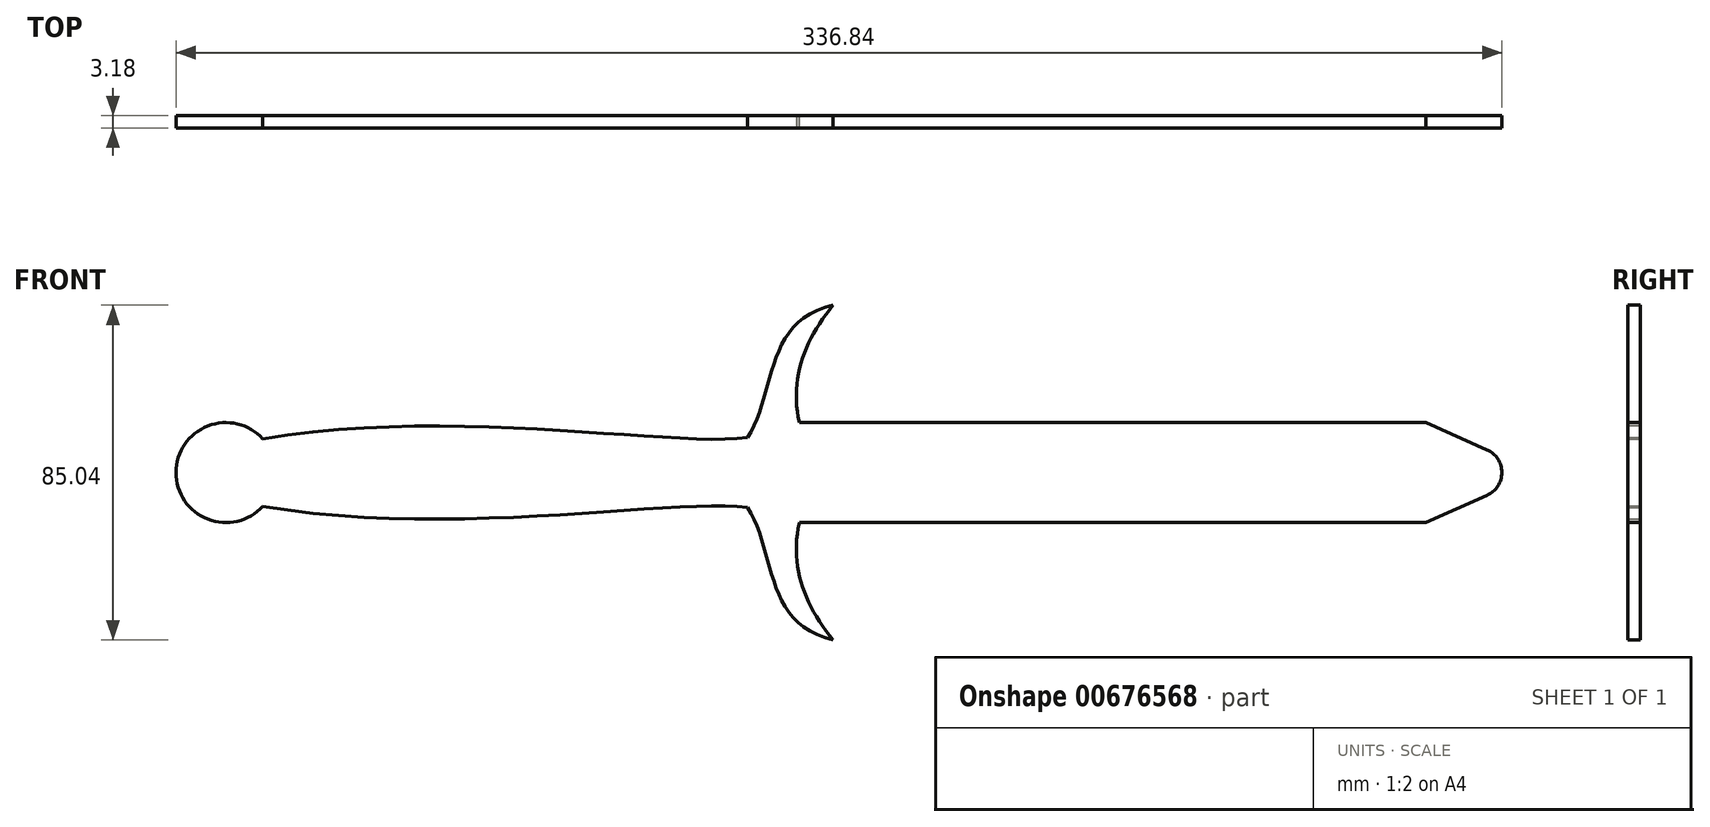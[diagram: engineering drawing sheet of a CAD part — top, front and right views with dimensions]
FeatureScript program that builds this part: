
annotation { "Feature Type Name" : "Feature", "Feature Type Description" : "" }
export const myFeature = defineFeature(function(context is Context, id is Id, definition is map)
    precondition{}
    {
        {
            var Q0;
            Q0=qCreatedBy(makeId("Front.planeOp"),FACE);
            var sketch = newSketch(context, id + "F0", { "sketchPlane" : qUnion([Q0])});
            skLineSegment(sketch, "E0", {"start": v(-145.25, 13.54) * mm, "end": v(159.55, 13.54) * mm, "construction": true});
            skCircle(sketch, "E1", {"center": v(-145.25, 13.54) * mm, "radius": 12.7 * mm});
            skFitSpline(sketch, "E2", {"points": [v(-135.87, 22.1) * mm, v(-12.7, 22.4) * mm], "startDerivative": vector(145, 25.04) * mm, "endDerivative": vector(57.12, 7.62) * mm});
            skFitSpline(sketch, "E3.MirrorCS", {"points": [v(-135.87, 4.98) * mm, v(-12.7, 4.67) * mm], "startDerivative": vector(145, -25.04) * mm, "endDerivative": vector(57.12, -7.62) * mm});
            skFitSpline(sketch, "E4", {"points": [v(-12.7, 22.4) * mm, v(9.02, 56.06) * mm], "startDerivative": vector(21.73, 33.66) * mm, "endDerivative": vector(53.2, 11.82) * mm});
            skFitSpline(sketch, "E5", {"points": [v(9.02, 56.06) * mm, v(3.11, 18.63) * mm], "startDerivative": vector(-27.07, -32.5) * mm, "endDerivative": vector(20.1, -42.56) * mm});
            skFitSpline(sketch, "E6.MirrorCS", {"points": [v(9.02, -28.98) * mm, v(3.11, 8.45) * mm], "startDerivative": vector(-27.07, 32.5) * mm, "endDerivative": vector(20.1, 42.56) * mm});
            skFitSpline(sketch, "E7.MirrorCS", {"points": [v(-12.7, 4.67) * mm, v(9.02, -28.98) * mm], "startDerivative": vector(21.73, -33.66) * mm, "endDerivative": vector(53.2, -11.82) * mm});
            skLineSegment(sketch, "E8", {"start": v(168.01, 26.24) * mm, "end": v(159.55, 26.24) * mm});
            skLineSegment(sketch, "E9", {"start": v(168.01, 26.24) * mm, "end": v(0.44, 26.24) * mm});
            skLineSegment(sketch, "E10", {"start": v(159.55, 26.24) * mm, "end": v(175.12, 19.35) * mm});
            skLineSegment(sketch, "E11.MirrorCS", {"start": v(168.01, 0.84) * mm, "end": v(0.44, 0.84) * mm});
            skLineSegment(sketch, "E12.MirrorCS", {"start": v(168.01, 0.84) * mm, "end": v(159.55, 0.84) * mm});
            skLineSegment(sketch, "E13.MirrorCS", {"start": v(159.55, 0.84) * mm, "end": v(175.12, 7.73) * mm});
            skPoint(sketch, "E14.visualSharp", {"position": v(188.23, 13.54) * mm});
            skArc(sketch, "E14.filletArc", {"start": v(175.12, 7.73) * mm, "mid": v(178.9, 13.54) * mm, "end": v(175.12, 19.35) * mm});
            skSolve(sketch);
        }
        {
            var Q0;
            {var subQ8=sQuery(id+"F0.wireOp",EDGE,"E2");Q0=makeQuery(id+"F0.imprint","IMPRINT",FACE,{"disambiguationData":[TD([[makeQuery(id+"F0.imprint","IMPRINT",EDGE,{"derivedFrom":subQ8}),-1.0]])]});}
            var Q1;
            {var subQ0=sQuery(id+"F0.wireOp",EDGE,"E1");var subQ1=makeQuery(id+"F0.imprint","INTERSECT",VERTEX,{"derivedFrom":[subQ0,sQuery(id+"F0.wireOp",EDGE,"E2")]});Q1=makeQuery(id+"F0.imprint","IMPRINT",FACE,{"disambiguationData":[TD([[makeQuery(id+"F0.imprint","IMPRINT",EDGE,{"disambiguationData":[TD([[subQ1,-1.0]])],"derivedFrom":subQ0}),1.0]])]});}
            extrude(context, id + "F1", {"entities" : qUnion([Q0, Q1]), "depth" : 3.17 * mm, "offsetDistance" : 25.4 * mm});
        }
    });
